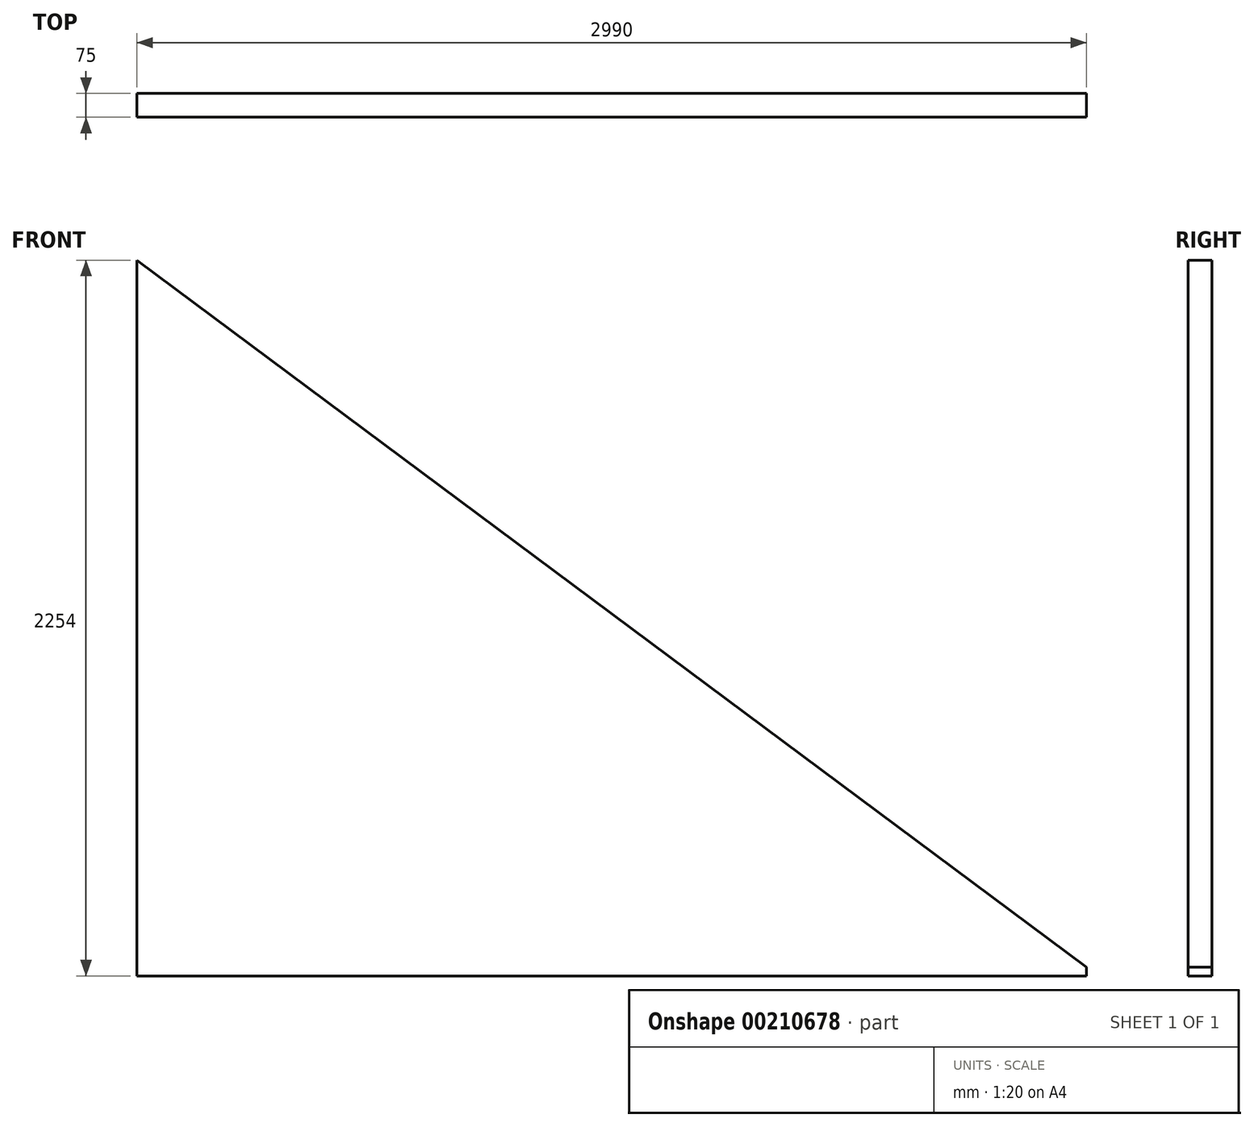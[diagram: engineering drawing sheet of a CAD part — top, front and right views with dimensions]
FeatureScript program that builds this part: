
annotation { "Feature Type Name" : "Feature", "Feature Type Description" : "" }
export const myFeature = defineFeature(function(context is Context, id is Id, definition is map)
    precondition{}
    {
        {
            var Q0;
            Q0=qCreatedBy(makeId("Front.planeOp"),FACE);
            var sketch = newSketch(context, id + "F0", { "sketchPlane" : qUnion([Q0])});
            skLineSegment(sketch, "E0.bottom", {"start": v(0, 0) * mm, "end": v(2990, 0) * mm});
            skLineSegment(sketch, "E0.left", {"start": v(0, 0) * mm, "end": v(0, 2254) * mm});
            skLineSegment(sketch, "E0.right", {"start": v(2990, 0) * mm, "end": v(2990, 27) * mm});
            skLineSegment(sketch, "E1", {"start": v(0, 2254) * mm, "end": v(2990, 27) * mm});
            skSolve(sketch);
        }
        {
            var Q0;
            Q0=makeQuery(id+"F0.imprint","IMPRINT",FACE,{"disambiguationData":[TD([[makeQuery(id+"F0.imprint","IMPRINT",EDGE,{"derivedFrom":sQuery(id+"F0.wireOp",EDGE,"E0.bottom")}),1.0]])]});
            extrude(context, id + "F1", {"entities" : qUnion([Q0]), "depth" : 75 * mm});
        }
    });
